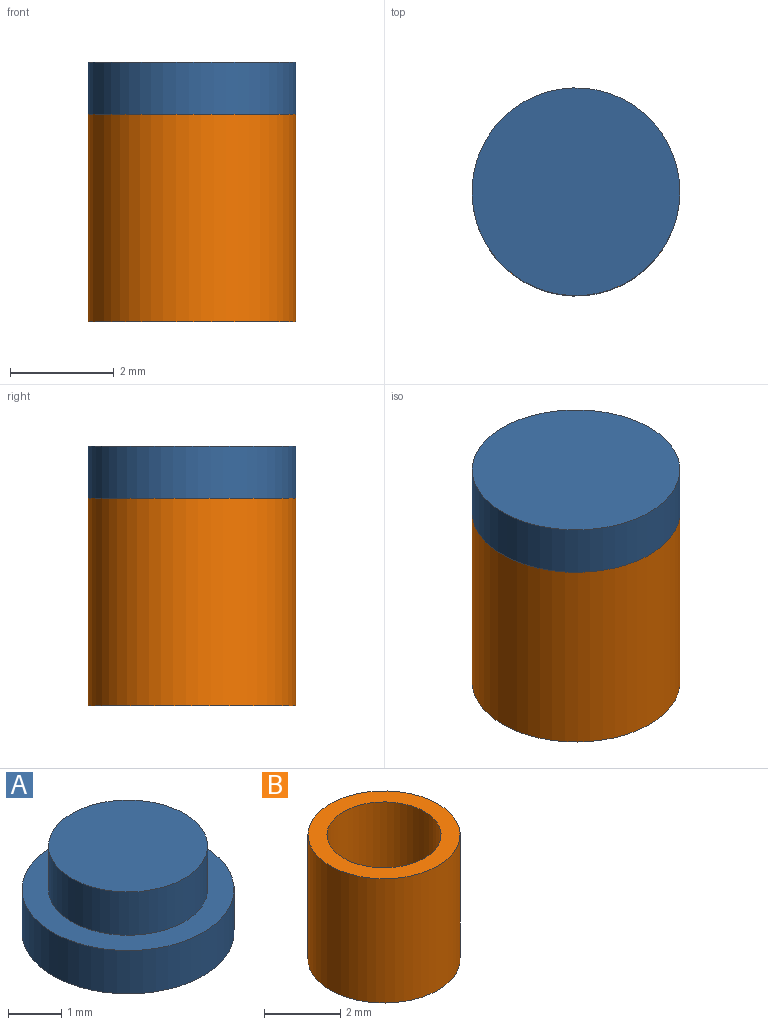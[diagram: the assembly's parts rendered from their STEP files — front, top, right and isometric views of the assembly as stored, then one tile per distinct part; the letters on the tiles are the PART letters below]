
ASSEMBLY  parts=2 mates=1
PART A: 5 faces, bbox 4x4x2 mm
  f0: cylinder r=2mm len=4mm, axis (0,0,-1), area 12.6mm2, adj f1,f2
  f1: plane 4x4mm, normal (0,0,1), area 5.5mm2, adj f0,f3
  f2: plane 4x4mm, normal (0,0,-1), area 12.6mm2, adj f0
  f3: cylinder r=1.5mm len=3mm, axis (0,0,-1), area 9.4mm2, adj f1,f4
  f4: plane 3x3mm, normal (0,0,1), area 7.1mm2, adj f3
PART B: 5 faces, bbox 4x4x4 mm
  f0: cylinder r=2mm len=4mm, axis (0,0,-1), area 50.3mm2, adj f1,f2
  f1: plane 4x4mm, normal (0,0,1), area 5.5mm2, adj f0,f4
  f2: plane 4x4mm, normal (0,0,-1), area 12.6mm2, adj f0
  f3: plane 3x3mm, normal (0,0,1), area 7.1mm2, adj f4
  f4: cylinder r=1.5mm len=3mm, axis (0,0,1), area 28.3mm2, adj f1,f3
PLACE A rot(axis=(1,0,0),180deg) t=(0,0,5)mm
PLACE B at identity
MATE slider A.f0 <-> B.f0  axis (0,0,1) through (0,0,4.5)mm
